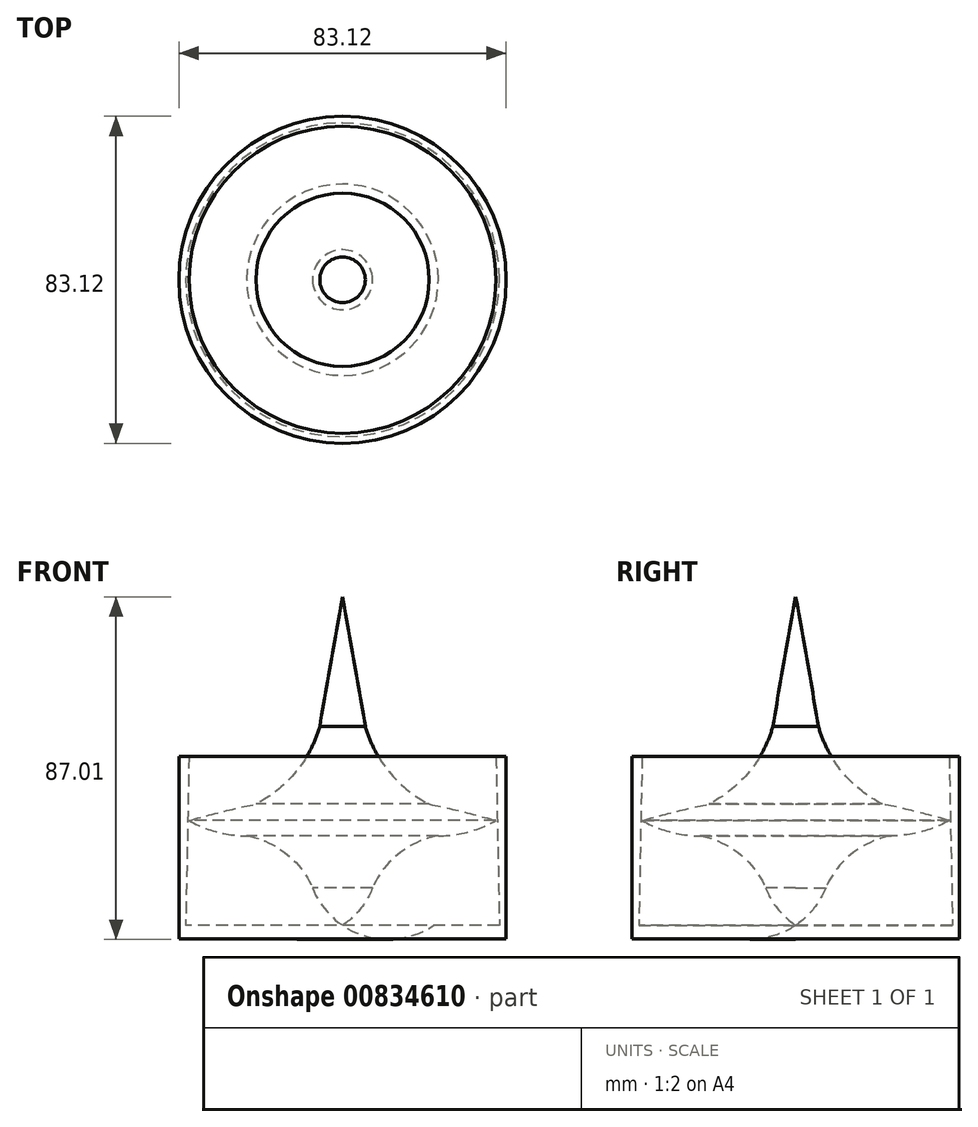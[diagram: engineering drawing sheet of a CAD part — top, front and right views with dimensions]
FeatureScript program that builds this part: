
annotation { "Feature Type Name" : "Feature", "Feature Type Description" : "" }
export const myFeature = defineFeature(function(context is Context, id is Id, definition is map)
    precondition{}
    {
        {
            var Q0;
            Q0=qCreatedBy(makeId("Front.planeOp"),FACE);
            var sketch = newSketch(context, id + "F0", { "sketchPlane" : qUnion([Q0])});
            skArc(sketch, "E0", {"start": v(-7.63, -17.12) * mm, "mid": v(-4.53, -22.45) * mm, "end": v(0, -26.62) * mm});
            skArc(sketch, "E1", {"start": v(-7.63, -17.12) * mm, "mid": v(-14.3, -8.4) * mm, "end": v(-24.32, -3.89) * mm});
            skArc(sketch, "E2", {"start": v(-39, 0) * mm, "mid": v(-31.9, -2.89) * mm, "end": v(-24.32, -3.89) * mm});
            skArc(sketch, "E3", {"start": v(-22.02, 4.17) * mm, "mid": v(-30.55, 2.25) * mm, "end": v(-39, 0) * mm});
            skArc(sketch, "E4", {"start": v(-22.02, 4.17) * mm, "mid": v(-11.84, 12.36) * mm, "end": v(-5.78, 23.92) * mm});
            skArc(sketch, "E5", {"start": v(0, 56.84) * mm, "mid": v(-2.96, 40.4) * mm, "end": v(-5.78, 23.92) * mm});
            skLineSegment(sketch, "E6", {"start": v(0, 56.84) * mm, "end": v(0, -26.62) * mm});
            skLineSegment(sketch, "E7", {"start": v(0, -26.62) * mm, "end": v(-39.86, -26.62) * mm});
            skLineSegment(sketch, "E8", {"start": v(-39.86, -26.62) * mm, "end": v(-39, 16.26) * mm});
            skLineSegment(sketch, "E9", {"start": v(0, -30.1) * mm, "end": v(0, -26.62) * mm});
            skLineSegment(sketch, "E10", {"start": v(0, -26.62) * mm, "end": v(0, -28.36) * mm});
            skLineSegment(sketch, "E11", {"start": v(0, -30.1) * mm, "end": v(-41.56, -30.1) * mm});
            skLineSegment(sketch, "E12", {"start": v(-41.56, -30.1) * mm, "end": v(-41.56, 16.26) * mm});
            skLineSegment(sketch, "E13", {"start": v(-41.56, 16.26) * mm, "end": v(-39, 16.26) * mm});
            skSolve(sketch);
        }
        {
            var Q0;
            Q0=makeQuery(id+"F0.imprint","IMPRINT",FACE,{"disambiguationData":[TD([[makeQuery(id+"F0.imprint","IMPRINT",EDGE,{"derivedFrom":sQuery(id+"F0.wireOp",EDGE,"E7")}),1.0]])]});
            var Q1;
            Q1=makeQuery(id+"F0.imprint","IMPRINT",FACE,{"disambiguationData":[TD([[makeQuery(id+"F0.imprint","IMPRINT",EDGE,{"derivedFrom":sQuery(id+"F0.wireOp",EDGE,"E0")}),1.0]])]});
            var Q2;
            Q2=sQuery(id+"F0.wireOp",EDGE,"E6");
            revolve(context, id + "F1", {"surfaceOperationType" : NewSurfaceOperationType.NEW, "entities" : qUnion([Q0, Q1]), "axis" : qUnion([Q2]), "revolveType" : RevolveType.FULL});
        }
    });
